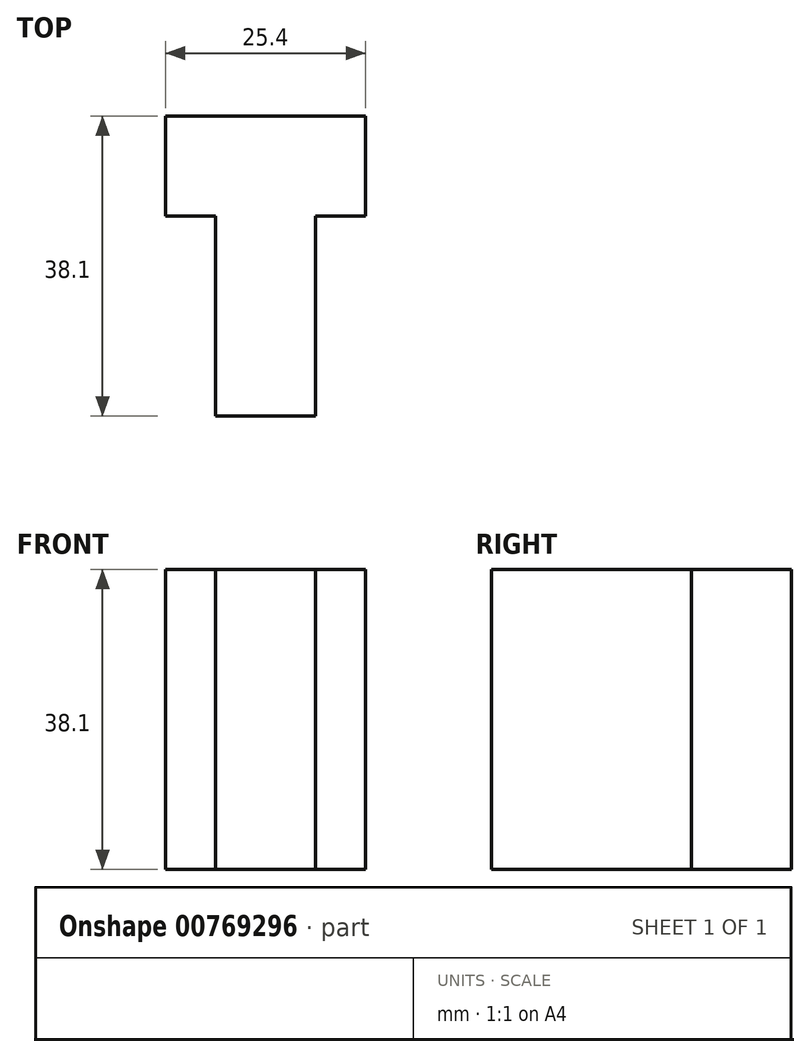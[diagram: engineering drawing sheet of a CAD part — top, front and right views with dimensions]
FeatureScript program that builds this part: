
annotation { "Feature Type Name" : "Feature", "Feature Type Description" : "" }
export const myFeature = defineFeature(function(context is Context, id is Id, definition is map)
    precondition{}
    {
        {
            var Q0;
            Q0=qCreatedBy(makeId("Top.planeOp"),FACE);
            var sketch = newSketch(context, id + "F0", { "sketchPlane" : qUnion([Q0])});
            skLineSegment(sketch, "E0", {"start": v(0, 0) * mm, "end": v(0, -25.4) * mm});
            skLineSegment(sketch, "E1", {"start": v(0, -25.4) * mm, "end": v(12.7, -25.4) * mm});
            skLineSegment(sketch, "E2", {"start": v(12.7, -25.4) * mm, "end": v(12.7, 0) * mm});
            skLineSegment(sketch, "E3", {"start": v(0, 0) * mm, "end": v(-6.35, 0) * mm});
            skLineSegment(sketch, "E4", {"start": v(-6.35, 0) * mm, "end": v(-6.35, 12.7) * mm});
            skLineSegment(sketch, "E5", {"start": v(-6.35, 12.7) * mm, "end": v(19.05, 12.7) * mm});
            skLineSegment(sketch, "E6", {"start": v(19.05, 12.7) * mm, "end": v(19.05, 0) * mm});
            skLineSegment(sketch, "E7", {"start": v(19.05, 0) * mm, "end": v(12.7, 0) * mm});
            skSolve(sketch);
        }
        {
            var Q0;
            Q0=makeQuery(id+"F0.imprint","IMPRINT",FACE,{"disambiguationData":[TD([[makeQuery(id+"F0.imprint","IMPRINT",EDGE,{"derivedFrom":sQuery(id+"F0.wireOp",EDGE,"E0")}),1.0]])]});
            extrude(context, id + "F1", {"entities" : qUnion([Q0]), "depth" : 38.1 * mm, "offsetDistance" : 25.4 * mm});
        }
    });
